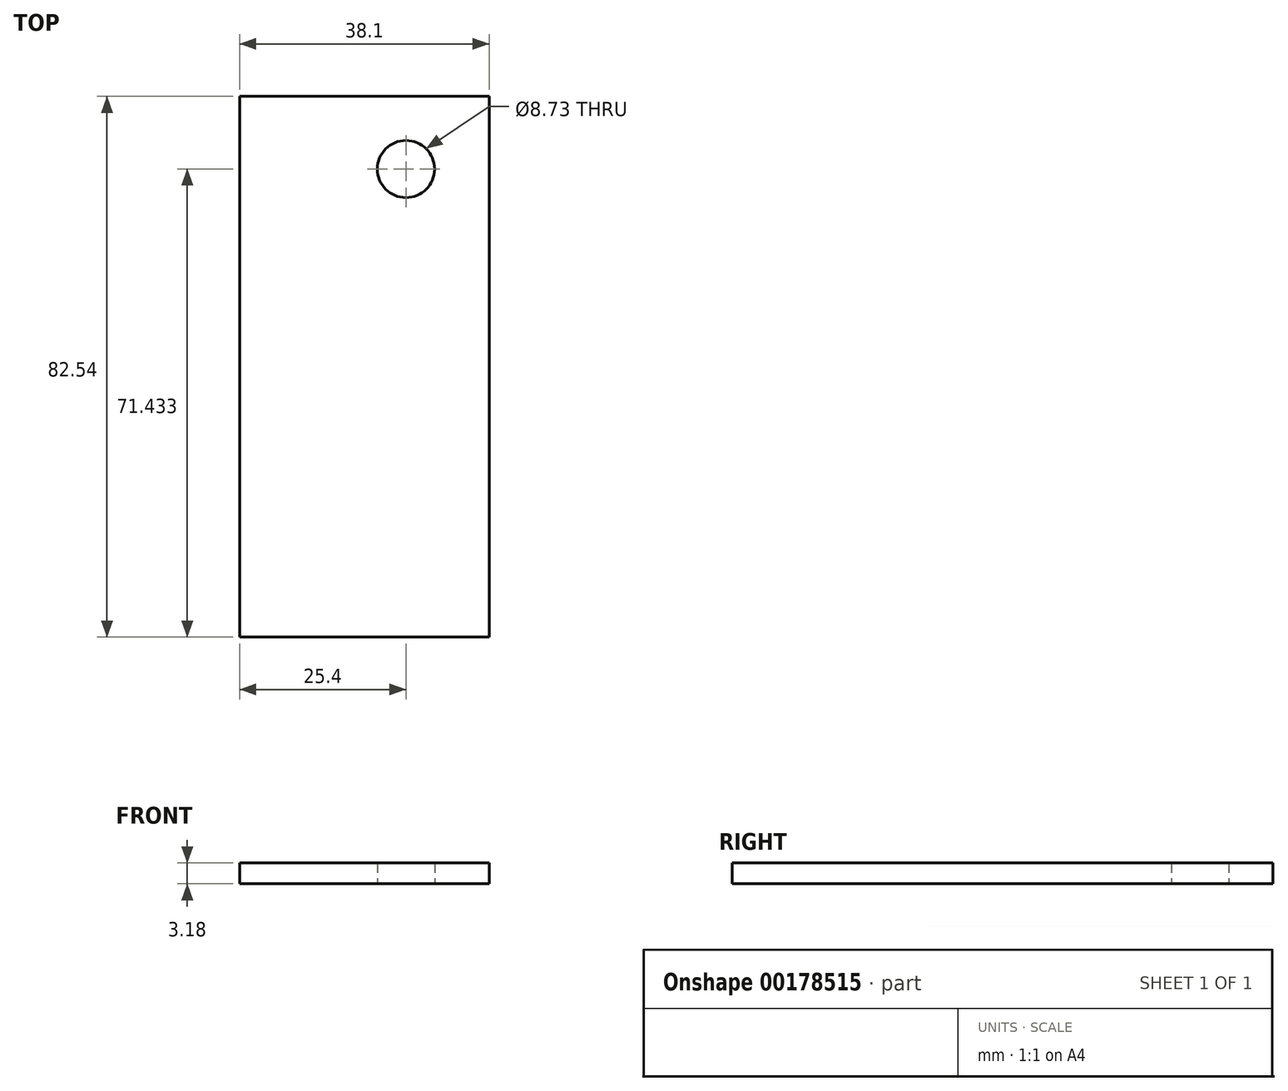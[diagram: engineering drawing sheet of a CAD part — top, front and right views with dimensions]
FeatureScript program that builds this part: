
annotation { "Feature Type Name" : "Feature", "Feature Type Description" : "" }
export const myFeature = defineFeature(function(context is Context, id is Id, definition is map)
    precondition{}
    {
        {
            var Q0;
            Q0=qCreatedBy(makeId("Top.planeOp"),FACE);
            var sketch = newSketch(context, id + "F0", { "sketchPlane" : qUnion([Q0])});
            skLineSegment(sketch, "E0.bottom", {"start": v(-19.05, 41.27) * mm, "end": v(19.05, 41.27) * mm});
            skLineSegment(sketch, "E0.top", {"start": v(-19.05, -41.28) * mm, "end": v(19.05, -41.28) * mm});
            skLineSegment(sketch, "E0.left", {"start": v(-19.05, 41.27) * mm, "end": v(-19.05, -41.28) * mm});
            skLineSegment(sketch, "E0.right", {"start": v(19.05, 41.27) * mm, "end": v(19.05, -41.28) * mm});
            skPoint(sketch, "E0.middle", {"position": v(0, 0) * mm});
            skCircle(sketch, "E1", {"center": v(6.35, 30.16) * mm, "radius": 4.37 * mm});
            skSolve(sketch);
        }
        {
            var Q0;
            Q0 = qSketchRegion(id + "F0", true);
            extrude(context, id + "F1", {"entities" : qUnion([Q0]), "depth" : 3.17 * mm});
        }
    });
